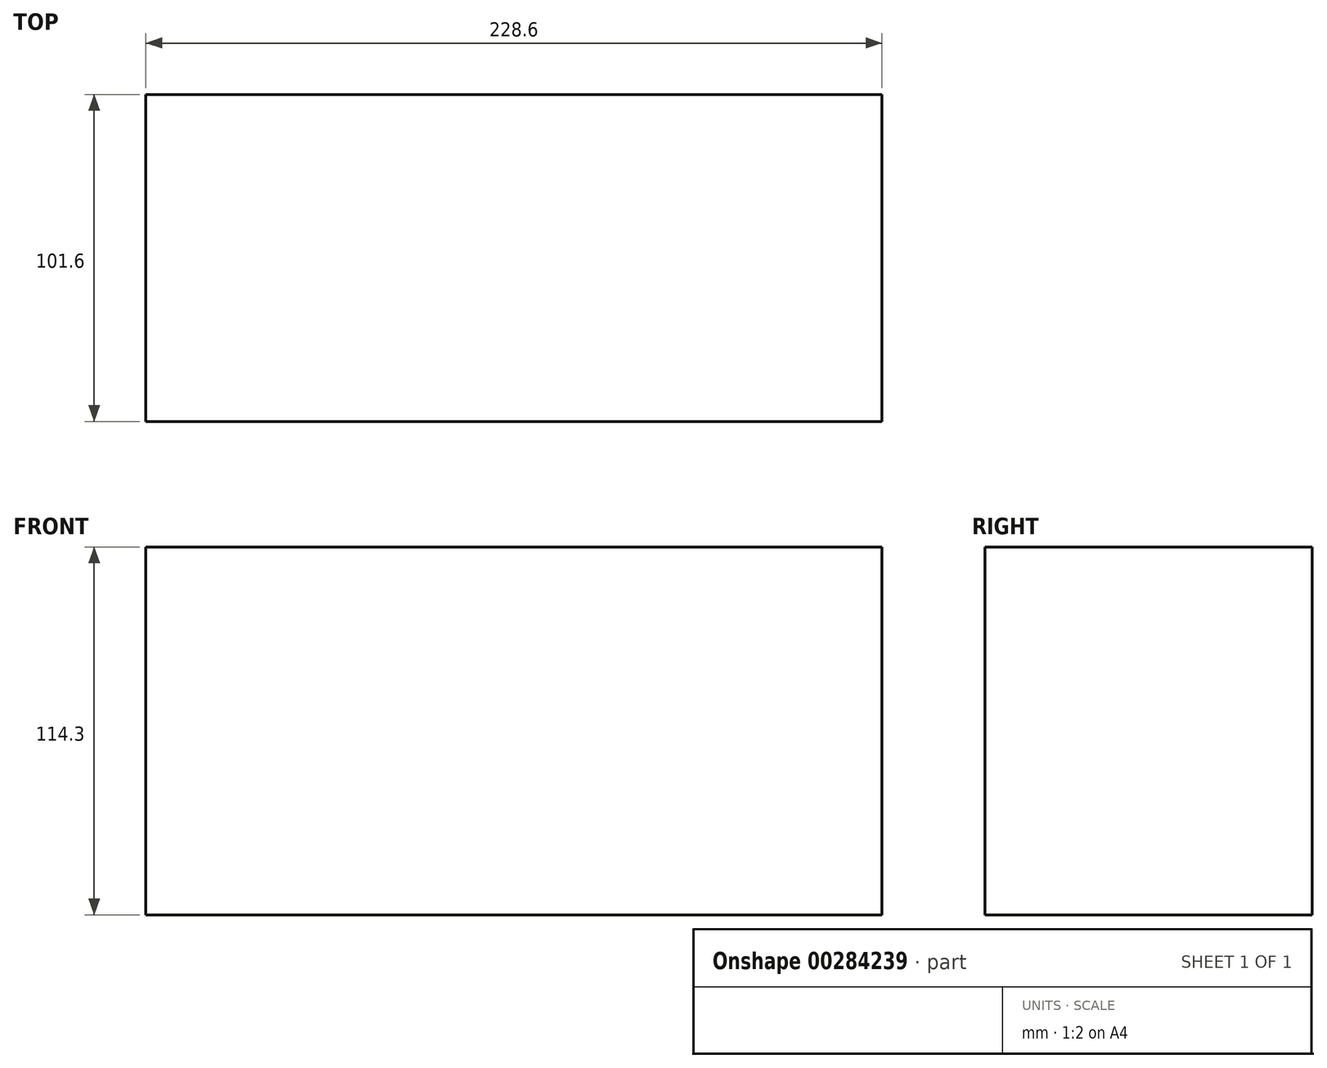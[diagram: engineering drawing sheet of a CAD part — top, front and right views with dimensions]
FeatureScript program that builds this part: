
annotation { "Feature Type Name" : "Feature", "Feature Type Description" : "" }
export const myFeature = defineFeature(function(context is Context, id is Id, definition is map)
    precondition{}
    {
        {
            var Q0;
            Q0=qCreatedBy(makeId("Front.planeOp"),FACE);
            var sketch = newSketch(context, id + "F0", { "sketchPlane" : qUnion([Q0])});
            skLineSegment(sketch, "E0.bottom", {"start": v(0, 0) * mm, "end": v(228.6, 0) * mm});
            skLineSegment(sketch, "E0.top", {"start": v(0, 114.3) * mm, "end": v(228.6, 114.3) * mm});
            skLineSegment(sketch, "E0.left", {"start": v(0, 0) * mm, "end": v(0, 114.3) * mm});
            skLineSegment(sketch, "E0.right", {"start": v(228.6, 0) * mm, "end": v(228.6, 114.3) * mm});
            skSolve(sketch);
        }
        {
            var Q0;
            Q0=makeQuery(id+"F0.imprint","IMPRINT",FACE,{"disambiguationData":[TD([[makeQuery(id+"F0.imprint","IMPRINT",EDGE,{"derivedFrom":sQuery(id+"F0.wireOp",EDGE,"E0.bottom")}),1.0]])]});
            extrude(context, id + "F1", {"entities" : qUnion([Q0]), "depth" : 101.6 * mm});
        }
    });
